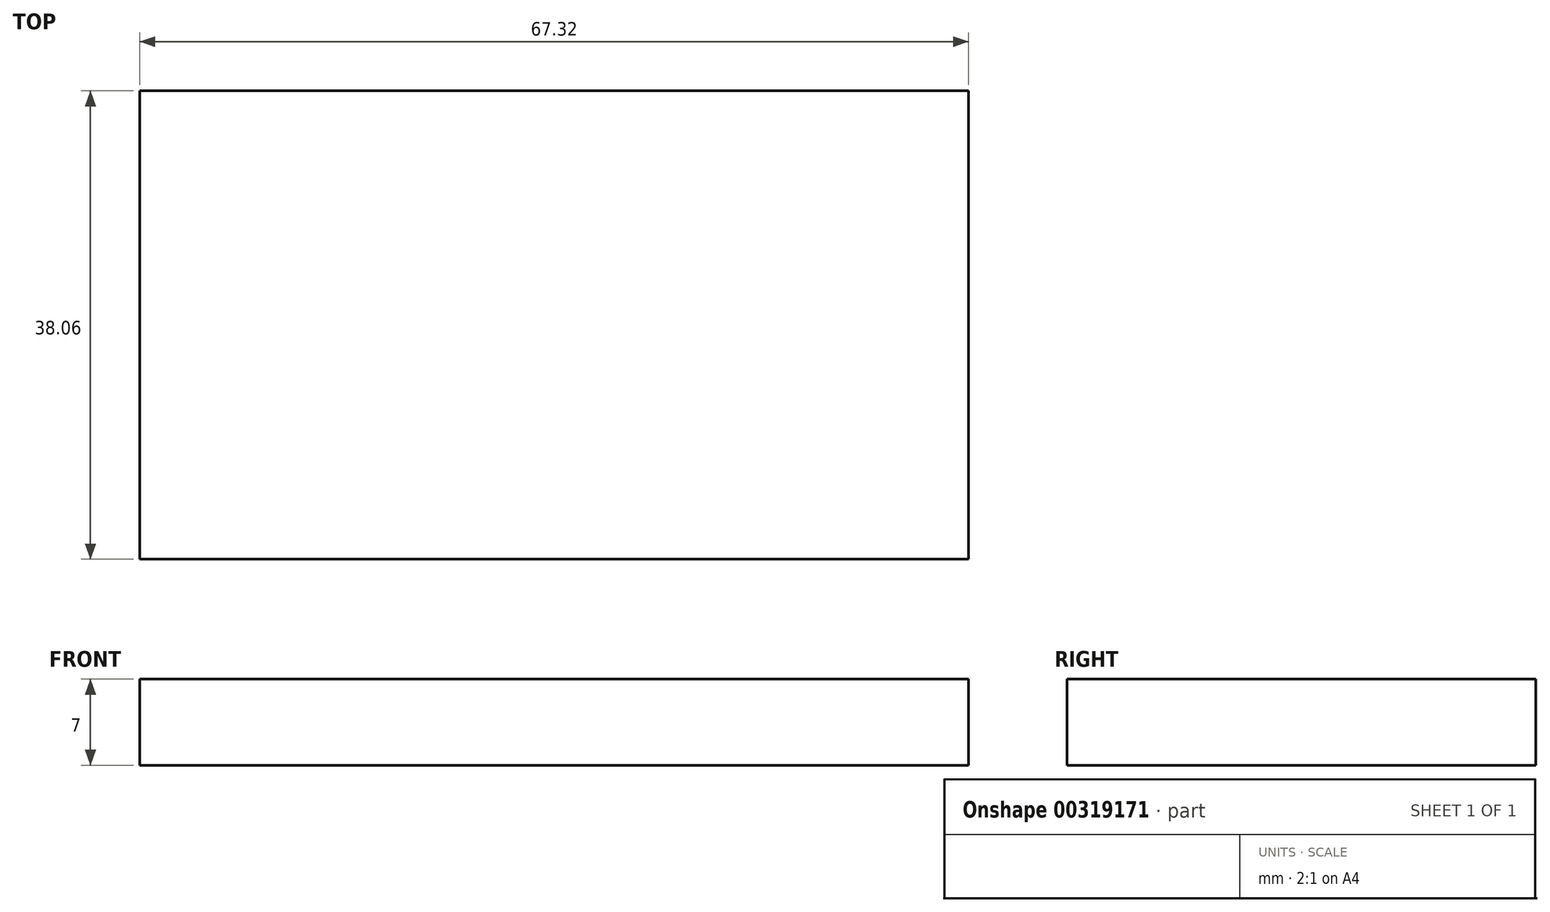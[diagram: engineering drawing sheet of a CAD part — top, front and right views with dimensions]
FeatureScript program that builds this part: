
annotation { "Feature Type Name" : "Feature", "Feature Type Description" : "" }
export const myFeature = defineFeature(function(context is Context, id is Id, definition is map)
    precondition{}
    {
        {
            var Q0;
            Q0=qCreatedBy(makeId("Top.planeOp"),FACE);
            var sketch = newSketch(context, id + "F0", { "sketchPlane" : qUnion([Q0])});
            skLineSegment(sketch, "E0.bottom", {"start": v(-37.8, 14.24) * mm, "end": v(29.52, 14.24) * mm});
            skLineSegment(sketch, "E0.top", {"start": v(-37.8, -23.82) * mm, "end": v(29.52, -23.82) * mm});
            skLineSegment(sketch, "E0.left", {"start": v(-37.8, 14.24) * mm, "end": v(-37.8, -23.82) * mm});
            skLineSegment(sketch, "E0.right", {"start": v(29.52, 14.24) * mm, "end": v(29.52, -23.82) * mm});
            skSolve(sketch);
        }
        {
            var Q0;
            Q0=makeQuery(id+"F0.imprint","IMPRINT",FACE,{"disambiguationData":[TD([[makeQuery(id+"F0.imprint","IMPRINT",EDGE,{"derivedFrom":sQuery(id+"F0.wireOp",EDGE,"E0.bottom")}),-1.0]])]});
            extrude(context, id + "F1", {"entities" : qUnion([Q0]), "depth" : 7 * mm});
        }
    });
